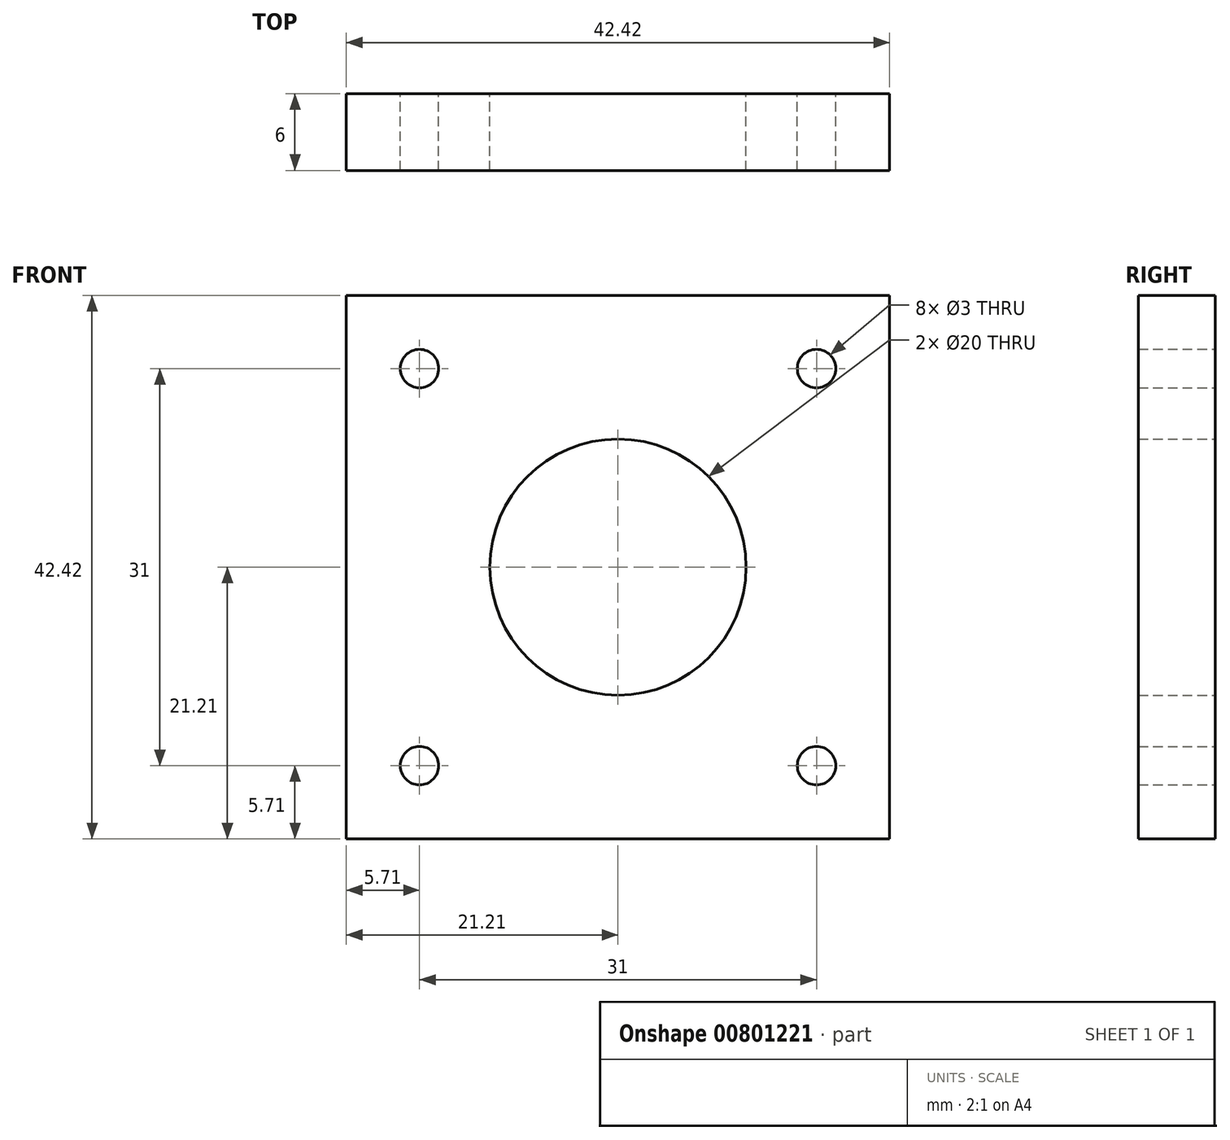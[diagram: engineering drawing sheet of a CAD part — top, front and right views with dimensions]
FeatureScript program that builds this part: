
annotation { "Feature Type Name" : "Feature", "Feature Type Description" : "" }
export const myFeature = defineFeature(function(context is Context, id is Id, definition is map)
    precondition{}
    {
        {
            var Q0;
            Q0=qCreatedBy(makeId("Front.planeOp"),FACE);
            var sketch = newSketch(context, id + "F0", { "sketchPlane" : qUnion([Q0])});
            skCircle(sketch, "E0", {"center": v(-15.5, 15.5) * mm, "radius": 1.5 * mm});
            skCircle(sketch, "E1", {"center": v(15.5, 15.5) * mm, "radius": 1.5 * mm});
            skCircle(sketch, "E2", {"center": v(15.5, -15.5) * mm, "radius": 1.5 * mm});
            skCircle(sketch, "E3", {"center": v(-15.5, -15.5) * mm, "radius": 1.5 * mm});
            skLineSegment(sketch, "E4", {"start": v(-45.72, 0) * mm, "end": v(49.85, 0) * mm, "construction": true});
            skLineSegment(sketch, "E5", {"start": v(0, -36.94) * mm, "end": v(0, 34.67) * mm, "construction": true});
            skLineSegment(sketch, "E6.rect.bottom", {"start": v(-15.5, 15.5) * mm, "end": v(15.5, 15.5) * mm, "construction": true});
            skLineSegment(sketch, "E6.rect.top", {"start": v(-15.5, -15.5) * mm, "end": v(15.5, -15.5) * mm, "construction": true});
            skLineSegment(sketch, "E6.rect.left", {"start": v(-15.5, 15.5) * mm, "end": v(-15.5, -15.5) * mm, "construction": true});
            skLineSegment(sketch, "E6.rect.right", {"start": v(15.5, 15.5) * mm, "end": v(15.5, -15.5) * mm, "construction": true});
            skPoint(sketch, "E6.rect.middle", {"position": v(0, 0) * mm});
            skPoint(sketch, "E7", {"position": v(0, 15.5) * mm});
            skSolve(sketch);
        }
        {
            assignVariable(context, id + "F1", {"name" : "Stepperblokjedikte", "anyValue" : 6});
        }
        {
            var Q0;
            Q0=qCreatedBy(makeId("Front.planeOp"),FACE);
            var sketch = newSketch(context, id + "F2", { "sketchPlane" : qUnion([Q0])});
            skLineSegment(sketch, "E8.bottom", {"start": v(-21.2, 21.2) * mm, "end": v(21.2, 21.2) * mm});
            skLineSegment(sketch, "E8.top", {"start": v(-21.2, -21.2) * mm, "end": v(21.2, -21.2) * mm});
            skLineSegment(sketch, "E8.left", {"start": v(-21.2, 21.2) * mm, "end": v(-21.2, -21.2) * mm});
            skLineSegment(sketch, "E8.right", {"start": v(21.2, 21.2) * mm, "end": v(21.2, -21.2) * mm});
            skCircle(sketch, "E9", {"center": v(-15.5, 15.5) * mm, "radius": 1.5 * mm});
            skCircle(sketch, "E10", {"center": v(15.5, 15.5) * mm, "radius": 1.5 * mm});
            skCircle(sketch, "E11", {"center": v(15.5, -15.5) * mm, "radius": 1.5 * mm});
            skCircle(sketch, "E12", {"center": v(-15.5, -15.5) * mm, "radius": 1.5 * mm});
            skLineSegment(sketch, "E13.rect.bottom", {"start": v(-15.5, 15.5) * mm, "end": v(15.5, 15.5) * mm, "construction": true});
            skLineSegment(sketch, "E13.rect.top", {"start": v(-15.5, -15.5) * mm, "end": v(15.5, -15.5) * mm, "construction": true});
            skLineSegment(sketch, "E13.rect.left", {"start": v(-15.5, 15.5) * mm, "end": v(-15.5, -15.5) * mm, "construction": true});
            skLineSegment(sketch, "E13.rect.right", {"start": v(15.5, 15.5) * mm, "end": v(15.5, -15.5) * mm, "construction": true});
            skPoint(sketch, "E13.rect.middle", {"position": v(0, 0) * mm});
            skPoint(sketch, "E14", {"position": v(0, 15.5) * mm});
            skCircle(sketch, "E15", {"center": v(0, 0) * mm, "radius": 10 * mm});
            skSolve(sketch);
        }
        {
            var Q0;
            Q0=qSketchRegion(id+"F2",true);
            extrude(context, id + "F3", {"entities" : qUnion([Q0]), "depth" : (getVariable(context, 'Stepperblokjedikte')) * mm, "offsetDistance" : 25 * mm});
        }
        {
            var Q0;
            Q0=makeQuery(id+"F3.opExtrude","SWEPT_BODY",BODY,{"disambiguationData":[OSD([sQuery(id+"F2.wireOp",EDGE,"E8.bottom"),sQuery(id+"F2.wireOp",EDGE,"E8.top"),sQuery(id+"F2.wireOp",EDGE,"E8.left"),sQuery(id+"F2.wireOp",EDGE,"E8.right"),sQuery(id+"F2.wireOp",EDGE,"E9"),sQuery(id+"F2.wireOp",EDGE,"E10"),sQuery(id+"F2.wireOp",EDGE,"E11"),sQuery(id+"F2.wireOp",EDGE,"E12"),sQuery(id+"F2.wireOp",EDGE,"E15")])]});
            transform(context, id + "F4", {"entities" : qUnion([Q0]), "transformType" : TransformType.TRANSLATION_3D, "dx" : 0 * mm, "dy" : 0 * mm, "dz" : 0 * mm, "makeCopy" : true});
        }
    });
